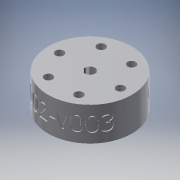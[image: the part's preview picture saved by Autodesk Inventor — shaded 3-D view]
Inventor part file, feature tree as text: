
AUTODESK INVENTOR PART (.ipt)
format: ipt  version: 2019.1 (Build 231200000, 200)  size: 3,056,640 bytes
history: native  units: mm
features: other x7, extrude x5, sketch x4, boolean_combine x1, plane x1, hole x1
ambient origin geometry x8: Origin, YZ Plane, XZ Plane, XY Plane, X Axis, Y Axis, Z Axis, Center Point
bodies: Solid1 (feature_tree), Solid3 (feature_tree)
feature tree (19):
  other  "MOT_WindowMotor_262100-3040.ipt"
  extrude  "Extrusion1"  Depth=30.0mm TaperAngle=0.0deg
  boolean_combine  "Combine2"
  other  "Thicken adapter hole"
  extrude  "Extrusion2"  Depth=10.0mm
  extrude  "Extrusion for middle hole"  Depth=20.0mm
  other  "Thicken Center Hole"
  extrude  "Extrusion for bolt holes"  Depth=35.0mm TaperAngle=0.0deg
  extrude  "Extrusion10"  Depth=35.0mm
  plane  "Work Plane1"
  other  "Emboss of part number"
  sketch  "Sketch1"  dims[d0=70.0mm d1=30.0mm d2=0.0mm]
  other  "Solid1::MOT_WindowMotor_262100-3040.ipt"
  other  "TaggingFeature2"
  other  "Smooth Base"
  hole  "Hole to view fit"  [1 undecoded]
  sketch  "Sketch14"  dims[d7=10.0mm d8=0.225mm d9=0.5mm]
  sketch  "Sketch for bolt holes"  dims[d10=70.0mm d11=20.0mm]
  sketch  "Sketch for part number"  dims[d12=2.0mm d13=0.0mm d22=3.0mm d23=0.0mm d44=0.2mm d45=0.01mm d66=6.858mm d67=25.4mm d68=60.0mm d70=360.0deg d72=30.0mm d73=0.0mm d74=11.3665mm d75=60.0mm d77=360.0deg d79=4.5mm d80=0.0mm d81=35.0mm d82=1.0mm d83=0.0mm d90=7.0mm]
note: 1 required parameter value undecoded (feature->parameter linkage not recoverable at this tier; creation-order binding heuristic only, values carry confidence <= 0.55)
